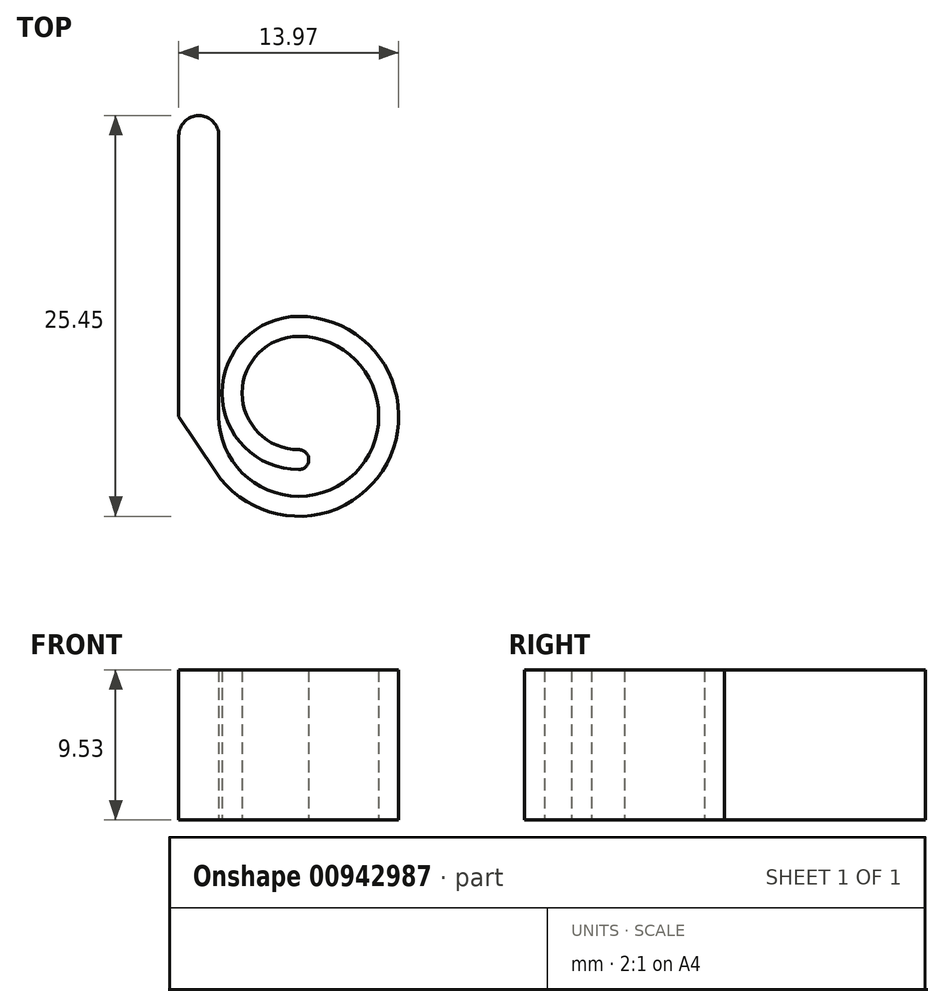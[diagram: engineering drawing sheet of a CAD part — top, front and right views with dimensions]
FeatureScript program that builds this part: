
annotation { "Feature Type Name" : "Feature", "Feature Type Description" : "" }
export const myFeature = defineFeature(function(context is Context, id is Id, definition is map)
    precondition{}
    {
        {
            var Q0;
            Q0=qCreatedBy(makeId("Top.planeOp"),FACE);
            var sketch = newSketch(context, id + "F0", { "sketchPlane" : qUnion([Q0])});
            skArc(sketch, "E0", {"start": v(-5.3, -3.51) * mm, "mid": v(5.6, -3) * mm, "end": v(0, 6.35) * mm});
            skArc(sketch, "E1", {"start": v(0, 6.35) * mm, "mid": v(-4.87, 1.48) * mm, "end": v(0, -3.38) * mm});
            skPoint(sketch, "E2.orphan", {"position": v(0, 3.89) * mm});
            skLineSegment(sketch, "E3.0", {"start": v(-5.08, 0) * mm, "end": v(-5.08, 17.83) * mm});
            skArc(sketch, "E4.0", {"start": v(-5.08, 0) * mm, "mid": v(3.6, -3.6) * mm, "end": v(0, 5.08) * mm});
            skArc(sketch, "E5.0", {"start": v(0, 5.08) * mm, "mid": v(-3.6, 1.48) * mm, "end": v(0, -2.11) * mm});
            skArc(sketch, "E6", {"start": v(0, -2.11) * mm, "mid": v(0.63, -2.75) * mm, "end": v(0, -3.38) * mm});
            skLineSegment(sketch, "E7.0", {"start": v(-7.62, 0) * mm, "end": v(-7.62, 17.83) * mm});
            skArc(sketch, "E8", {"start": v(-7.62, 17.83) * mm, "mid": v(-6.35, 19.1) * mm, "end": v(-5.08, 17.83) * mm});
            skLineSegment(sketch, "E9", {"start": v(-7.62, 0) * mm, "end": v(-5.3, -3.51) * mm});
            skPoint(sketch, "E10.orphan", {"position": v(-6.35, 0) * mm});
            skSolve(sketch);
        }
        {
            var Q0;
            Q0=qSketchRegion(id+"F0",true);
            extrude(context, id + "F1", {"entities" : qUnion([Q0]), "depth" : 9.52 * mm, "offsetDistance" : 25.4 * mm});
        }
    });
